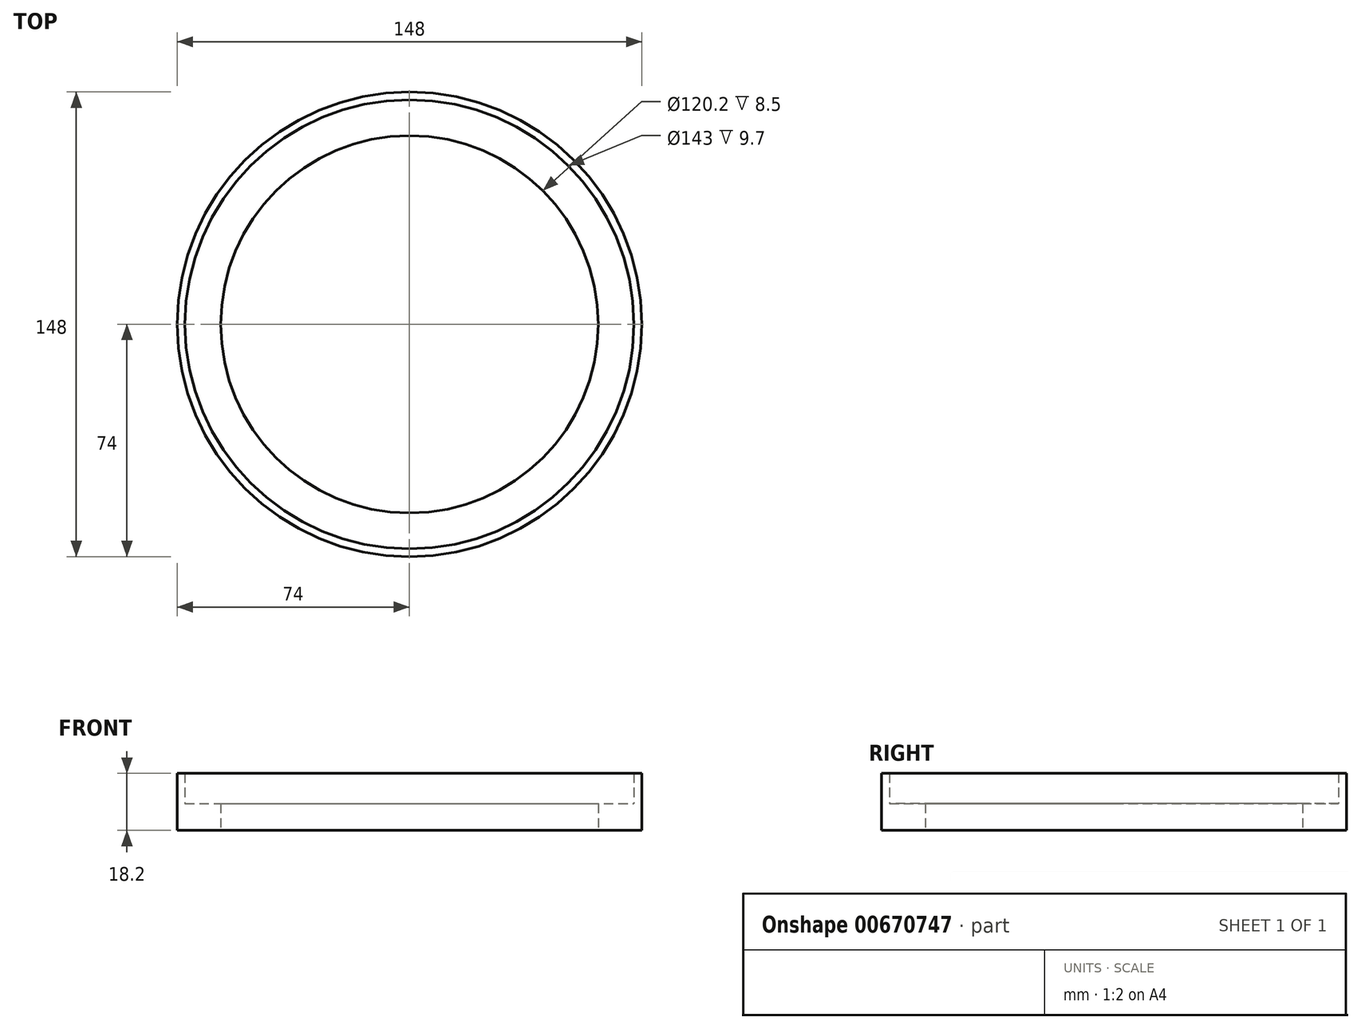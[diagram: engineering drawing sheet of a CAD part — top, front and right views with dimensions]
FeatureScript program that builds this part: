
annotation { "Feature Type Name" : "Feature", "Feature Type Description" : "" }
export const myFeature = defineFeature(function(context is Context, id is Id, definition is map)
    precondition{}
    {
        {
            var Q0;
            Q0=qCreatedBy(makeId("Front.planeOp"),FACE);
            var sketch = newSketch(context, id + "F0", { "sketchPlane" : qUnion([Q0])});
            skLineSegment(sketch, "E0", {"start": v(60.1, 0) * mm, "end": v(74, 0) * mm});
            skLineSegment(sketch, "E1", {"start": v(74, 0) * mm, "end": v(74, 18.2) * mm});
            skLineSegment(sketch, "E2", {"start": v(74, 18.2) * mm, "end": v(71.5, 18.2) * mm});
            skLineSegment(sketch, "E3", {"start": v(71.5, 18.2) * mm, "end": v(71.5, 8.5) * mm});
            skLineSegment(sketch, "E4", {"start": v(71.5, 8.5) * mm, "end": v(60.1, 8.5) * mm});
            skLineSegment(sketch, "E5", {"start": v(60.1, 8.5) * mm, "end": v(60.1, 0) * mm});
            skLineSegment(sketch, "E6", {"start": v(0, 0) * mm, "end": v(0, 23.63) * mm, "construction": true});
            skSolve(sketch);
        }
        {
            var Q0;
            Q0=makeQuery(id+"F0.imprint","IMPRINT",FACE,{"disambiguationData":[TD([[makeQuery(id+"F0.imprint","IMPRINT",EDGE,{"derivedFrom":sQuery(id+"F0.wireOp",EDGE,"E0")}),1.0]])]});
            var Q1;
            Q1=sQuery(id+"F0.wireOp",EDGE,"E6");
            revolve(context, id + "F1", {"entities" : qUnion([Q0]), "axis" : qUnion([Q1]), "revolveType" : RevolveType.FULL});
        }
    });
